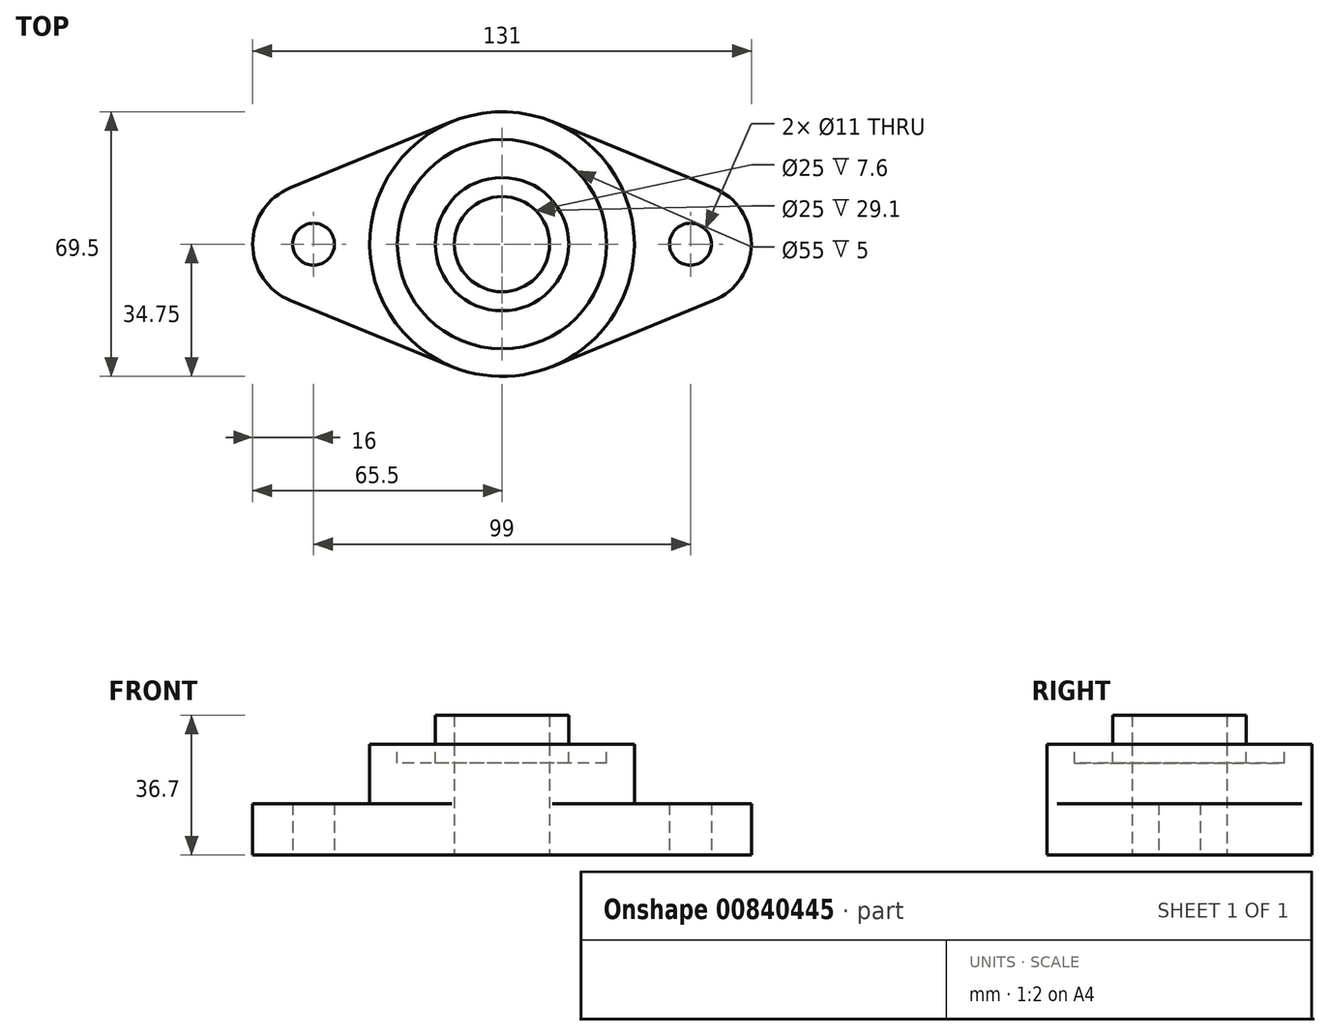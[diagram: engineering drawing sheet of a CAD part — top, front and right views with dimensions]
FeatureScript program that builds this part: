
annotation { "Feature Type Name" : "Feature", "Feature Type Description" : "" }
export const myFeature = defineFeature(function(context is Context, id is Id, definition is map)
    precondition{}
    {
        {
            var Q0;
            Q0=qCreatedBy(makeId("Top.planeOp"),FACE);
            var sketch = newSketch(context, id + "F0", { "sketchPlane" : qUnion([Q0])});
            skLineSegment(sketch, "E0", {"start": v(-65.5, 0) * mm, "end": v(65.5, 0) * mm, "construction": true});
            skCircle(sketch, "E1", {"center": v(0, 0) * mm, "radius": 34.75 * mm});
            skCircle(sketch, "E2", {"center": v(49.5, 0) * mm, "radius": 5.5 * mm});
            skCircle(sketch, "E3", {"center": v(-49.5, 0) * mm, "radius": 5.5 * mm});
            skLineSegment(sketch, "E4", {"start": v(-55.56, 14.8) * mm, "end": v(-13.16, 32.16) * mm});
            skLineSegment(sketch, "E5", {"start": v(13.16, 32.16) * mm, "end": v(55.56, 14.8) * mm});
            skLineSegment(sketch, "E6", {"start": v(55.56, -14.8) * mm, "end": v(13.16, -32.16) * mm});
            skLineSegment(sketch, "E7", {"start": v(-13.16, -32.16) * mm, "end": v(-55.56, -14.8) * mm});
            skCircle(sketch, "E8", {"center": v(0, 0) * mm, "radius": 12.5 * mm});
            skArc(sketch, "E9.trimOffspring", {"start": v(55.56, -14.8) * mm, "mid": v(65.5, 0) * mm, "end": v(55.56, 14.8) * mm});
            skArc(sketch, "E10.trimOffspring", {"start": v(-55.56, 14.8) * mm, "mid": v(-65.5, 0) * mm, "end": v(-55.56, -14.8) * mm});
            skSolve(sketch);
        }
        {
            var Q0;
            Q0 = qSketchRegion(id + "F0", true);
            extrude(context, id + "F1", {"entities" : qUnion([Q0]), "depth" : 13.5 * mm, "offsetDistance" : 25 * mm});
        }
        {
            var Q0;
            Q0=makeQuery(id+"F1.opExtrude","CAP_FACE",FACE,{"disambiguationData":[OSD([sQuery(id+"F0.wireOp",EDGE,"E1"),sQuery(id+"F0.wireOp",EDGE,"E2"),sQuery(id+"F0.wireOp",EDGE,"E3"),sQuery(id+"F0.wireOp",EDGE,"E4"),sQuery(id+"F0.wireOp",EDGE,"E5"),sQuery(id+"F0.wireOp",EDGE,"E6"),sQuery(id+"F0.wireOp",EDGE,"E7"),sQuery(id+"F0.wireOp",EDGE,"E8"),sQuery(id+"F0.wireOp",EDGE,"E9.trimOffspring"),sQuery(id+"F0.wireOp",EDGE,"E10.trimOffspring")])],"isStart":false});
            var sketch = newSketch(context, id + "F2", { "sketchPlane" : qUnion([Q0])});
            skCircle(sketch, "E11", {"center": v(0, 0) * mm, "radius": 34.75 * mm});
            skCircle(sketch, "E12", {"center": v(0, 0) * mm, "radius": 12.5 * mm});
            skSolve(sketch);
        }
        {
            var Q0;
            Q0 = qSketchRegion(id + "F2", true);
            extrude(context, id + "F3", {"entities" : qUnion([Q0]), "operationType" : NewBodyOperationType.ADD, "depth" : (29.1 - 13.5) * mm, "offsetDistance" : 25 * mm});
        }
        {
            var Q0;
            Q0=makeQuery(id+"F3.opExtrude","CAP_FACE",FACE,{"disambiguationData":[OSD([sQuery(id+"F2.wireOp",EDGE,"E11"),sQuery(id+"F2.wireOp",EDGE,"E12")])],"isStart":false});
            var sketch = newSketch(context, id + "F4", { "sketchPlane" : qUnion([Q0])});
            skCircle(sketch, "E13", {"center": v(0, 0) * mm, "radius": 17.5 * mm});
            skCircle(sketch, "E14", {"center": v(0, 0) * mm, "radius": 12.5 * mm});
            skSolve(sketch);
        }
        {
            var Q0;
            Q0 = qSketchRegion(id + "F4", true);
            extrude(context, id + "F5", {"entities" : qUnion([Q0]), "depth" : (36.7 - 29.1) * mm, "offsetDistance" : 25 * mm});
        }
        {
            var Q0;
            Q0=makeQuery(id+"F3.opExtrude","CAP_FACE",FACE,{"disambiguationData":[OSD([sQuery(id+"F2.wireOp",EDGE,"E11"),sQuery(id+"F2.wireOp",EDGE,"E12")])],"isStart":false});
            var sketch = newSketch(context, id + "F6", { "sketchPlane" : qUnion([Q0])});
            skCircle(sketch, "E15", {"center": v(0, 0) * mm, "radius": 17.5 * mm});
            skCircle(sketch, "E16.0", {"center": v(0, 0) * mm, "radius": 27.5 * mm});
            skSolve(sketch);
        }
        {
            var Q0;
            Q0 = qSketchRegion(id + "F6", true);
            extrude(context, id + "F7", {"entities" : qUnion([Q0]), "operationType" : NewBodyOperationType.REMOVE, "oppositeDirection" : true, "depth" : 5 * mm, "offsetDistance" : 25 * mm});
        }
    });
